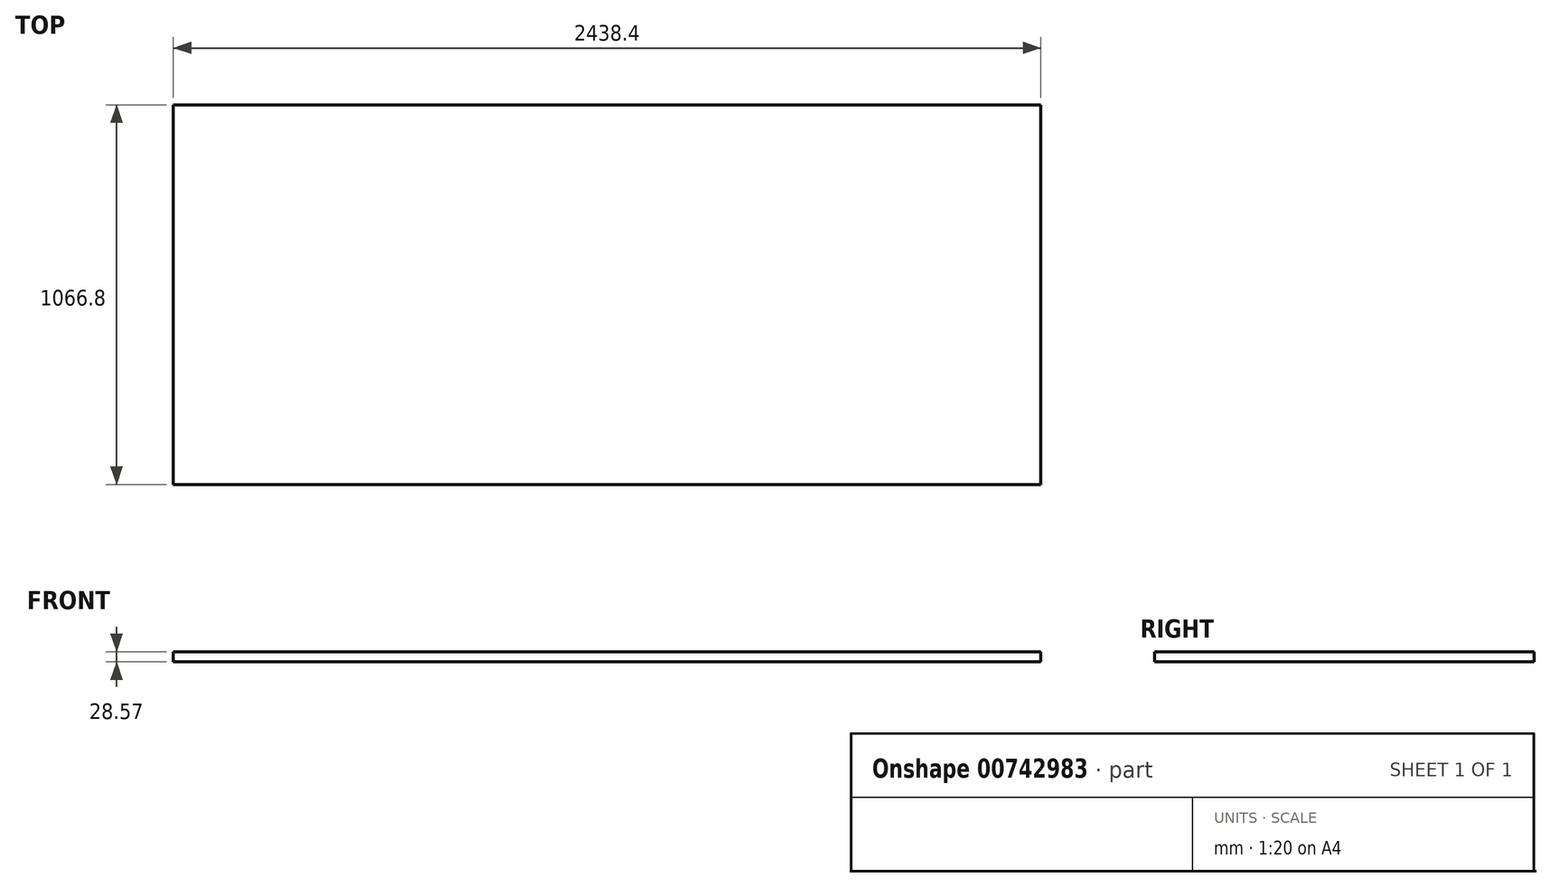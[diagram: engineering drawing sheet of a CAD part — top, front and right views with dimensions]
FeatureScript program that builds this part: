
annotation { "Feature Type Name" : "Feature", "Feature Type Description" : "" }
export const myFeature = defineFeature(function(context is Context, id is Id, definition is map)
    precondition{}
    {
        {
            var Q0;
            Q0=qCreatedBy(makeId("Top.planeOp"),FACE);
            var sketch = newSketch(context, id + "F0", { "sketchPlane" : qUnion([Q0])});
            skLineSegment(sketch, "E0.bottom", {"start": v(1219.2, 533.4) * mm, "end": v(-1219.2, 533.4) * mm});
            skLineSegment(sketch, "E0.top", {"start": v(1219.2, -533.4) * mm, "end": v(-1219.2, -533.4) * mm});
            skLineSegment(sketch, "E0.left", {"start": v(1219.2, 533.4) * mm, "end": v(1219.2, -533.4) * mm});
            skLineSegment(sketch, "E0.right", {"start": v(-1219.2, 533.4) * mm, "end": v(-1219.2, -533.4) * mm});
            skPoint(sketch, "E0.middle", {"position": v(0, 0) * mm});
            skSolve(sketch);
        }
        {
            var Q0;
            Q0=makeQuery(id+"F0.imprint","IMPRINT",FACE,{"disambiguationData":[TD([[makeQuery(id+"F0.imprint","IMPRINT",EDGE,{"derivedFrom":sQuery(id+"F0.wireOp",EDGE,"E0.bottom")}),1.0]])]});
            extrude(context, id + "F1", {"entities" : qUnion([Q0]), "depth" : 28.57 * mm, "offsetDistance" : 25.4 * mm});
        }
    });
